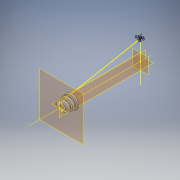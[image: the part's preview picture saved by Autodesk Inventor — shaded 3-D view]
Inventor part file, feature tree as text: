
AUTODESK INVENTOR PART (.ipt)
format: ipt  version: 2018 (Build 220112000, 112)  size: 339,456 bytes
history: native  units: in
note: dims shown in document units (in); Inventor stores cm internally (conversion verified against a paired STEP export)
features: sketch x4, helix x2, plane x1, loft x1, hole x1, other x1, extrude x1, projected_geometry x1
ambient origin geometry x8: Origin, YZ Plane, XZ Plane, XY Plane, X Axis, Y Axis, Z Axis, Center Point
bodies: Solid1 (feature_tree)
feature tree (12):
  sketch  "Sketch1"  dims[d0=2.0in d2=3.9in]
  plane  "Work Plane1"
  loft  "Loft1"
  hole  "Hole1"  [1 undecoded]
  other  "Work Axis2"
  sketch  "Sketch6"  dims[d11=0.16in d12=0.75in d13=0.375in d14=0.25in d15=0.5635in d16=1.0in d17=0.8108in d41=0.1in]
  helix  "Coil3"  [1 undecoded]
  helix  "Coil4"  [1 undecoded]
  extrude  "Extrusion2"  Depth=1.0in
  sketch  "Sketch2"  dims[d3=0.5in d5=0.0in d6=90.0deg d7=0.0in d8=90.0deg d9=1.0in d10=1.0in]
  projected_geometry  "Projected Loop1"
  sketch  "Sketch8"  dims[d42=0.1in d43=0.02in d44=0.195in d45=1.0in d46=7.874in d47=-0.0739in d48=90.0deg d49=90.0deg d50=0.0in d51=0.0in d52=0.195in d53=1.0in d54=7.874in d55=0.0756in d56=90.0deg d57=90.0deg d58=0.0in d59=0.0in d60=3.4in d61=3.0in d62=0.0in]
note: 3 required parameter values undecoded (feature->parameter linkage not recoverable at this tier; creation-order binding heuristic only, values carry confidence <= 0.55)
